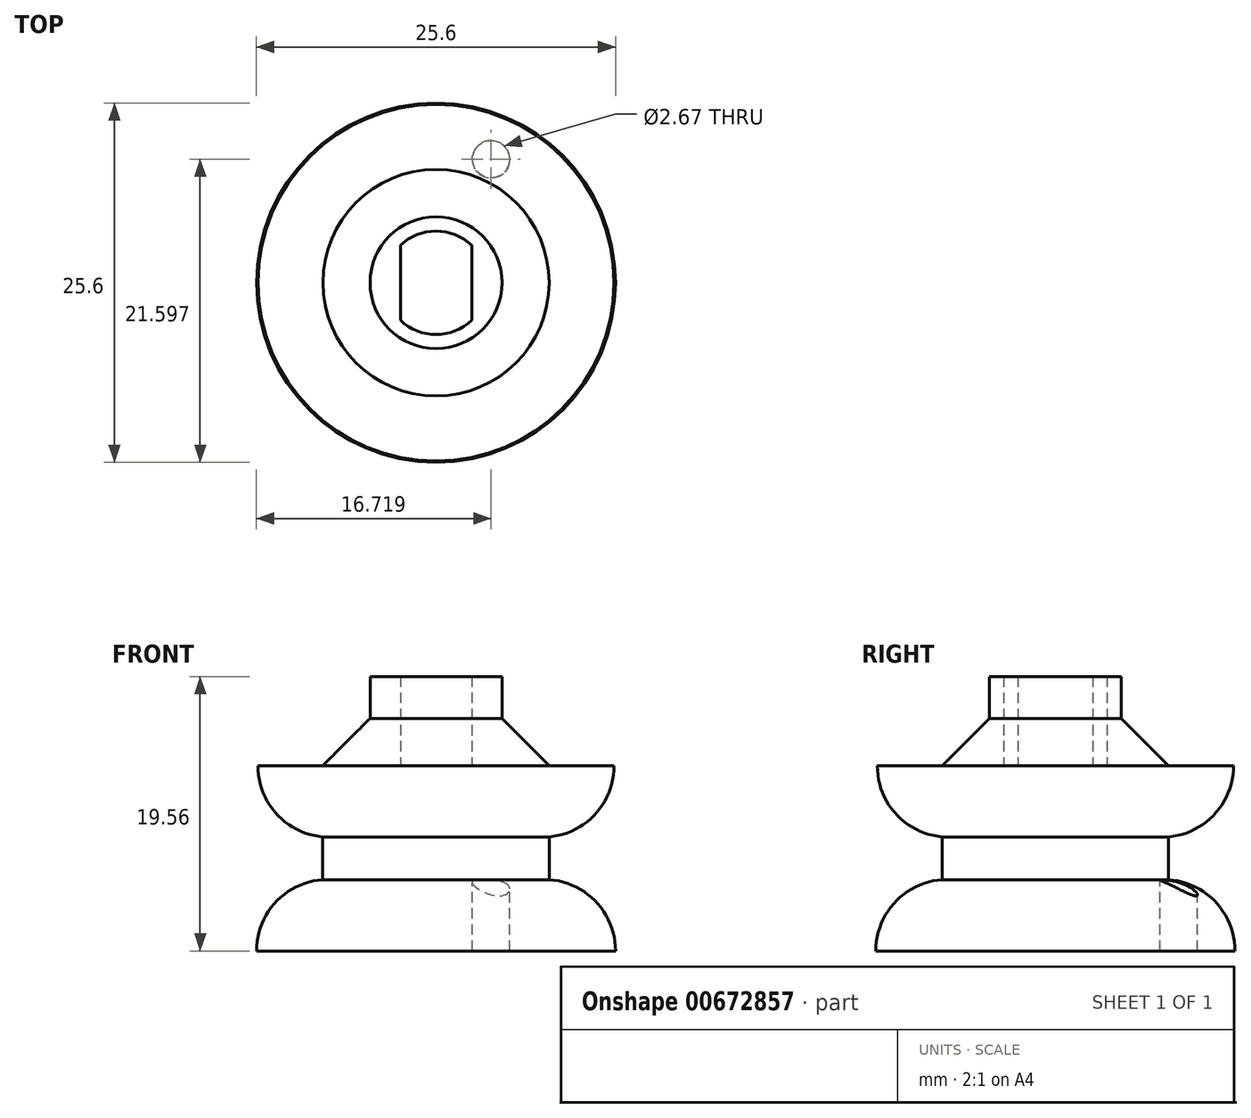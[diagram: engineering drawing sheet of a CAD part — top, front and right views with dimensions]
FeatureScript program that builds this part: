
annotation { "Feature Type Name" : "Feature", "Feature Type Description" : "" }
export const myFeature = defineFeature(function(context is Context, id is Id, definition is map)
    precondition{}
    {
        {
            var Q0;
            Q0=qCreatedBy(makeId("Top.planeOp"),FACE);
            var sketch = newSketch(context, id + "F0", { "sketchPlane" : qUnion([Q0])});
            skCircle(sketch, "E0", {"center": v(0, 0) * mm, "radius": 4.7 * mm});
            skCircle(sketch, "E1", {"center": v(0, 0) * mm, "radius": 3.68 * mm});
            skLineSegment(sketch, "E2", {"start": v(0, 0) * mm, "end": v(-2.54, 0) * mm});
            skLineSegment(sketch, "E3", {"start": v(0, 0) * mm, "end": v(2.54, 0) * mm});
            skLineSegment(sketch, "E4.bottom", {"start": v(2.54, 2.67) * mm, "end": v(3.77, 2.67) * mm});
            skLineSegment(sketch, "E4.top", {"start": v(2.54, -2.8) * mm, "end": v(3.77, -2.8) * mm});
            skLineSegment(sketch, "E4.left", {"start": v(2.54, 2.67) * mm, "end": v(2.54, -2.8) * mm});
            skLineSegment(sketch, "E4.right", {"start": v(3.77, 2.67) * mm, "end": v(3.77, -2.8) * mm});
            skLineSegment(sketch, "E5.bottom", {"start": v(-2.54, 2.67) * mm, "end": v(-3.77, 2.67) * mm});
            skLineSegment(sketch, "E5.top", {"start": v(-2.54, -2.8) * mm, "end": v(-3.77, -2.8) * mm});
            skLineSegment(sketch, "E5.left", {"start": v(-2.54, 2.67) * mm, "end": v(-2.54, -2.8) * mm});
            skLineSegment(sketch, "E5.right", {"start": v(-3.77, 2.67) * mm, "end": v(-3.77, -2.8) * mm});
            skCircle(sketch, "E6", {"center": v(0, 0) * mm, "radius": 8.06 * mm});
            skSolve(sketch);
        }
        {
            var Q0;
            {var subQ1=sQuery(id+"F0.wireOp",EDGE,"E4.top");Q0=makeQuery(id+"F0.imprint","IMPRINT",FACE,{"disambiguationData":[TD([[makeQuery(id+"F0.imprint","IMPRINT",EDGE,{"derivedFrom":subQ1}),-1.0]])]});}
            var Q1;
            {var subQ0=sQuery(id+"F0.wireOp",EDGE,"E4.left");var subQ4=makeQuery(id+"F0.imprint","INTERSECT",VERTEX,{"derivedFrom":[sQuery(id+"F0.wireOp",EDGE,"E3"),subQ0]});Q1=makeQuery(id+"F0.imprint","IMPRINT",FACE,{"disambiguationData":[TD([[makeQuery(id+"F0.imprint","IMPRINT",EDGE,{"disambiguationData":[TD([[subQ4,-1.0]])],"derivedFrom":subQ0}),1.0]])]});}
            var Q2;
            {var subQ4=sQuery(id+"F0.wireOp",EDGE,"E4.bottom");Q2=makeQuery(id+"F0.imprint","IMPRINT",FACE,{"disambiguationData":[TD([[makeQuery(id+"F0.imprint","IMPRINT",EDGE,{"derivedFrom":subQ4}),-1.0]])]});}
            var Q3;
            {var subQ1=sQuery(id+"F0.wireOp",EDGE,"E4.bottom");Q3=makeQuery(id+"F0.imprint","IMPRINT",FACE,{"disambiguationData":[TD([[makeQuery(id+"F0.imprint","IMPRINT",EDGE,{"derivedFrom":subQ1}),1.0]])]});}
            var Q4;
            {var subQ1=sQuery(id+"F0.wireOp",EDGE,"E5.bottom");Q4=makeQuery(id+"F0.imprint","IMPRINT",FACE,{"disambiguationData":[TD([[makeQuery(id+"F0.imprint","IMPRINT",EDGE,{"derivedFrom":subQ1}),1.0]])]});}
            var Q5;
            {var subQ0=sQuery(id+"F0.wireOp",EDGE,"E5.left");var subQ4=makeQuery(id+"F0.imprint","INTERSECT",VERTEX,{"derivedFrom":[sQuery(id+"F0.wireOp",EDGE,"E2"),subQ0]});Q5=makeQuery(id+"F0.imprint","IMPRINT",FACE,{"disambiguationData":[TD([[makeQuery(id+"F0.imprint","IMPRINT",EDGE,{"disambiguationData":[TD([[subQ4,-1.0]])],"derivedFrom":subQ0}),-1.0]])]});}
            extrude(context, id + "F1", {"entities" : qUnion([Q0, Q1, Q2, Q3, Q4, Q5]), "depth" : 6.35 * mm, "offsetDistance" : 25.4 * mm});
        }
        {
            var Q0;
            Q0=qCreatedBy(makeId("Top.planeOp"),FACE);
            var sketch = newSketch(context, id + "F2", { "sketchPlane" : qUnion([Q0])});
            skCircle(sketch, "E7", {"center": v(0, 0) * mm, "radius": 12.7 * mm});
            skCircle(sketch, "E8", {"center": v(0, 0) * mm, "radius": 8.07 * mm});
            skSolve(sketch);
        }
        {
            var Q0;
            Q0=makeQuery(id+"F2.imprint","IMPRINT",FACE,{"disambiguationData":[TD([[makeQuery(id+"F2.imprint","IMPRINT",EDGE,{"derivedFrom":sQuery(id+"F2.wireOp",EDGE,"E7")}),1.0]])]});
            var Q1;
            Q1=sQuery(id+"F2.wireOp",EDGE,"E7");
            extrude(context, id + "F3", {"entities" : qUnion([Q0]), "operationType" : NewBodyOperationType.ADD, "surfaceEntities" : qUnion([Q1]), "oppositeDirection" : true, "depth" : 5.08 * mm, "offsetDistance" : 25.4 * mm});
        }
        {
            var Q0;
            Q0=makeQuery(id+"F2.imprint","IMPRINT",FACE,{"disambiguationData":[TD([[makeQuery(id+"F2.imprint","IMPRINT",EDGE,{"derivedFrom":sQuery(id+"F2.wireOp",EDGE,"E8")}),1.0]])]});
            extrude(context, id + "F4", {"entities" : qUnion([Q0]), "operationType" : NewBodyOperationType.ADD, "oppositeDirection" : true, "depth" : 8.13 * mm, "offsetDistance" : 25.4 * mm});
        }
        {
            var Q0;
            Q0=makeQuery(id+"F4.opExtrude","CAP_FACE",FACE,{"disambiguationData":[OSD([sQuery(id+"F2.wireOp",EDGE,"E8")])],"isStart":false});
            var sketch = newSketch(context, id + "F5", { "sketchPlane" : qUnion([Q0])});
            skCircle(sketch, "E9", {"center": v(0, 0) * mm, "radius": 12.8 * mm});
            skCircle(sketch, "E10", {"center": v(3.92, -8.8) * mm, "radius": 1.34 * mm});
            skSolve(sketch);
        }
        {
            var Q0;
            Q0=makeQuery(id+"F5.imprint","IMPRINT",FACE,{"disambiguationData":[TD([[makeQuery(id+"F5.imprint","IMPRINT",EDGE,{"derivedFrom":sQuery(id+"F5.wireOp",EDGE,"E9")}),1.0]])]});
            var Q1;
            Q1=makeQuery(id+"F5.imprint","IMPRINT",FACE,{"disambiguationData":[TD([[makeQuery(id+"F5.imprint","IMPRINT",EDGE,{"derivedFrom":makeQuery(id+"F4.opExtrude","CAP_EDGE",EDGE,{"disambiguationData":[OSD([sQuery(id+"F2.wireOp",EDGE,"E8")])],"isStart":false})}),-1.0]])]});
            extrude(context, id + "F6", {"entities" : qUnion([Q0, Q1]), "operationType" : NewBodyOperationType.ADD, "depth" : 5.08 * mm, "offsetDistance" : 25.4 * mm});
        }
        {
            var Q0;
            Q0=makeQuery(id+"F6.opExtrude","CAP_EDGE",EDGE,{"disambiguationData":[OSD([sQuery(id+"F5.wireOp",EDGE,"E9")])],"isStart":true});
            var Q1;
            Q1=makeQuery(id+"F3.opExtrude","CAP_EDGE",EDGE,{"disambiguationData":[OSD([sQuery(id+"F2.wireOp",EDGE,"E7")])],"isStart":false});
            fillet(context, id + "F7", {"entities" : qUnion([Q0, Q1]), "radius" : 5.08 * mm, "tangentPropagation" : true, "allowEdgeOverflow" : false});
        }
        {
            var Q0;
            Q0=makeQuery(id+"F0.imprint","IMPRINT",FACE,{"disambiguationData":[TD([[makeQuery(id+"F0.imprint","IMPRINT",EDGE,{"derivedFrom":sQuery(id+"F0.wireOp",EDGE,"E6")}),1.0]])]});
            extrude(context, id + "F8", {"entities" : qUnion([Q0]), "operationType" : NewBodyOperationType.ADD, "depth" : 3.8 * mm, "offsetDistance" : 25.4 * mm});
        }
        {
            var Q0;
            Q0=makeQuery(id+"F8.opExtrude","CAP_EDGE",EDGE,{"disambiguationData":[OSD([sQuery(id+"F0.wireOp",EDGE,"E6")])],"isStart":false});
            chamfer(context, id + "F9", {"entities" : qUnion([Q0]), "width" : 3.8 * mm, "tangentPropagation" : true});
        }
    });
